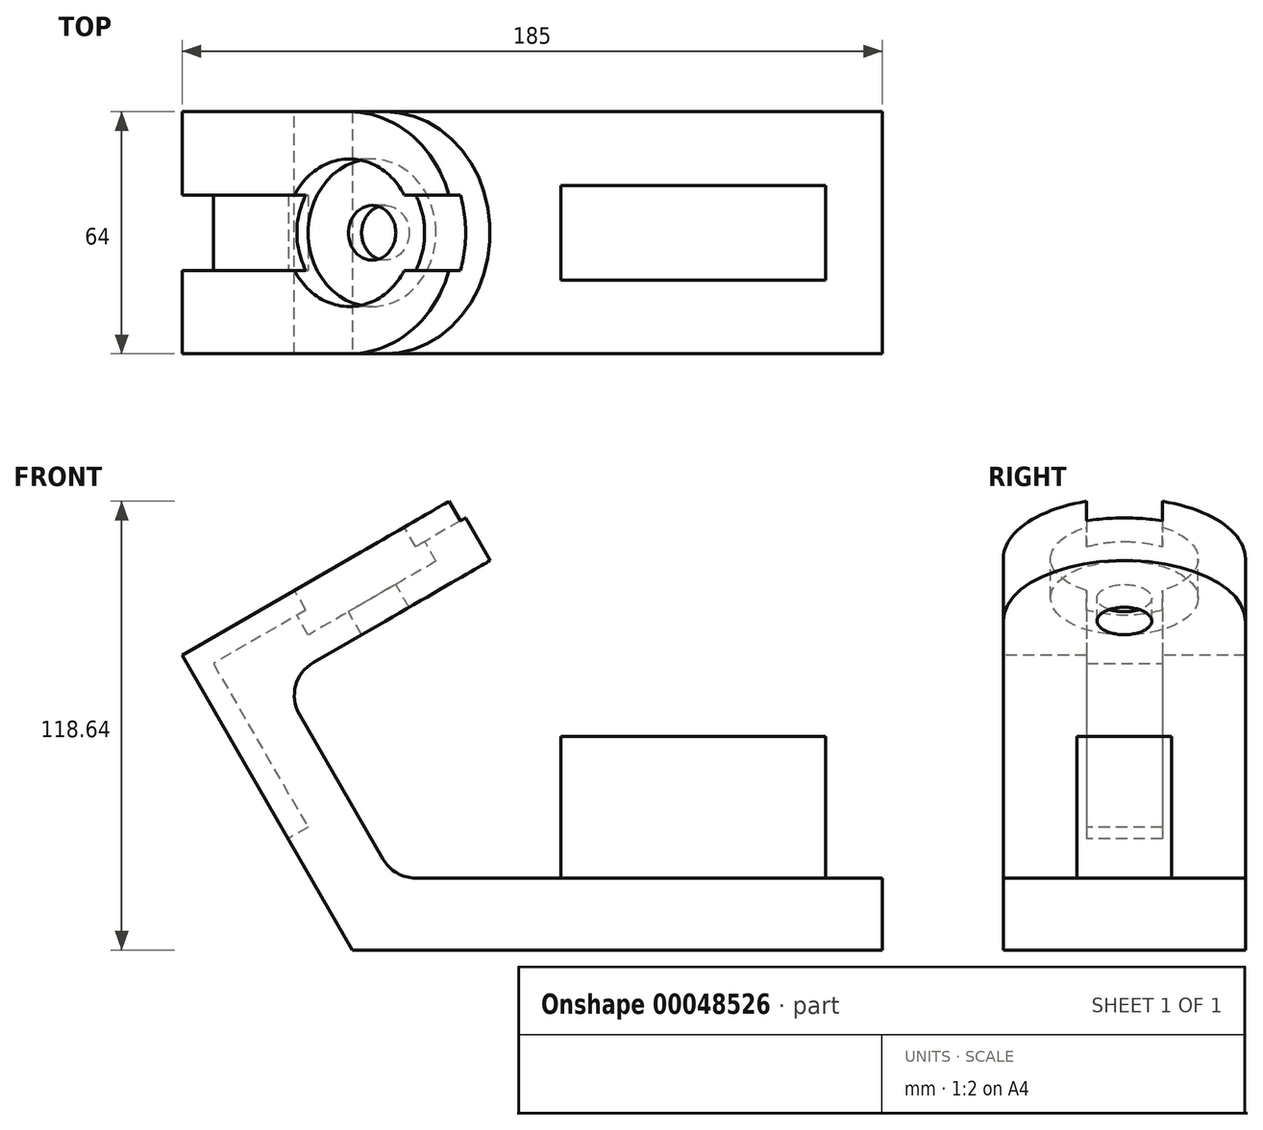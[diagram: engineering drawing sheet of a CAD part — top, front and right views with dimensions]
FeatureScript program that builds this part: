
annotation { "Feature Type Name" : "Feature", "Feature Type Description" : "" }
export const myFeature = defineFeature(function(context is Context, id is Id, definition is map)
    precondition{}
    {
        {
            var Q0;
            Q0=qCreatedBy(makeId("Front.planeOp"),FACE);
            var sketch = newSketch(context, id + "F0", { "sketchPlane" : qUnion([Q0])});
            skLineSegment(sketch, "E0", {"start": v(0, 0) * mm, "end": v(-45, 77.94) * mm});
            skLineSegment(sketch, "E1", {"start": v(-45, 77.94) * mm, "end": v(26.88, 119.44) * mm});
            skLineSegment(sketch, "E2", {"start": v(0, 0) * mm, "end": v(140, 0) * mm});
            skLineSegment(sketch, "E3.0", {"start": v(-19.05, 70.99) * mm, "end": v(36.38, 102.99) * mm});
            skLineSegment(sketch, "E3.1", {"start": v(10.97, 19) * mm, "end": v(-19.05, 70.99) * mm});
            skLineSegment(sketch, "E3.2", {"start": v(10.97, 19) * mm, "end": v(140, 19) * mm});
            skLineSegment(sketch, "E4", {"start": v(26.88, 119.44) * mm, "end": v(36.38, 102.99) * mm});
            skLineSegment(sketch, "E5", {"start": v(140, 0) * mm, "end": v(140, 19) * mm});
            skSolve(sketch);
        }
        {
            var Q0;
            Q0 = qSketchRegion(id + "F0", true);
            extrude(context, id + "F1", {"entities" : qUnion([Q0]), "oppositeDirection" : true, "depth" : 64 * mm});
        }
        {
            var Q0;
            Q0=makeQuery(id+"F1.opExtrude","SWEPT_FACE",FACE,{"disambiguationData":[OSD([sQuery(id+"F0.wireOp",EDGE,"E1")])]});
            var sketch = newSketch(context, id + "F2", { "sketchPlane" : qUnion([Q0])});
            skCircle(sketch, "E6", {"center": v(51, 32) * mm, "radius": 32 * mm});
            skSolve(sketch);
        }
        {
            var Q0;
            {var subQ0=sQuery(id+"F0.wireOp",EDGE,"E1");var subQ2=sQuery(id+"F2.wireOp",EDGE,"E6");var subQ4=makeQuery(id+"F1.opExtrude","CAP_EDGE",EDGE,{"disambiguationData":[OSD([subQ0])],"isStart":false});var subQ6=makeQuery(id+"F2.imprint","INTERSECT",VERTEX,{"derivedFrom":[subQ4,subQ2]});Q0=makeQuery(id+"F2.imprint","IMPRINT",FACE,{"disambiguationData":[TD([[makeQuery(id+"F2.imprint","IMPRINT",EDGE,{"disambiguationData":[TD([[subQ6,1.0]])],"derivedFrom":subQ2}),-1.0]])]});}
            var Q1;
            {var subQ0=sQuery(id+"F0.wireOp",EDGE,"E1");var subQ1=makeQuery(id+"F1.opExtrude","CAP_EDGE",EDGE,{"disambiguationData":[OSD([subQ0])],"isStart":true});var subQ2=sQuery(id+"F2.wireOp",EDGE,"E6");var subQ3=makeQuery(id+"F2.imprint","INTERSECT",VERTEX,{"derivedFrom":[subQ1,subQ2]});Q1=makeQuery(id+"F2.imprint","IMPRINT",FACE,{"disambiguationData":[TD([[makeQuery(id+"F2.imprint","IMPRINT",EDGE,{"disambiguationData":[TD([[subQ3,-1.0]])],"derivedFrom":subQ2}),-1.0]])]});}
            extrude(context, id + "F3", {"entities" : qUnion([Q0, Q1]), "operationType" : NewBodyOperationType.REMOVE, "oppositeDirection" : true, "depth" : 25 * mm});
        }
        {
            var Q0;
            Q0=makeQuery(id+"F1.opExtrude","SWEPT_FACE",FACE,{"disambiguationData":[OSD([sQuery(id+"F0.wireOp",EDGE,"E1")])]});
            var sketch = newSketch(context, id + "F4", { "sketchPlane" : qUnion([Q0])});
            skCircle(sketch, "E7", {"center": v(51, 32) * mm, "radius": 19.5 * mm});
            skCircle(sketch, "E8", {"center": v(51, 32) * mm, "radius": 6 * mm});
            skSolve(sketch);
        }
        {
            var Q0;
            Q0 = qSketchRegion(id + "F4", true);
            var Q1;
            Q1=makeQuery(id+"F4.imprint","IMPRINT",FACE,{"disambiguationData":[TD([[makeQuery(id+"F4.imprint","IMPRINT",EDGE,{"derivedFrom":sQuery(id+"F4.wireOp",EDGE,"E8")}),1.0]])]});
            var Q2;
            Q2=makeQuery(id+"F4.imprint","IMPRINT",FACE,{"disambiguationData":[TD([[makeQuery(id+"F4.imprint","IMPRINT",EDGE,{"derivedFrom":sQuery(id+"F4.wireOp",EDGE,"E7")}),1.0]])]});
            extrude(context, id + "F5", {"entities" : qUnion([Q0, Q1, Q2]), "operationType" : NewBodyOperationType.REMOVE, "oppositeDirection" : true, "depth" : 12 * mm});
        }
        {
            var Q0;
            Q0=makeQuery(id+"F5.boolean.opBoolean","COPY",FACE,{"derivedFrom":makeQuery(id+"F5.opExtrude","CAP_FACE",FACE,{"disambiguationData":[OSD([sQuery(id+"F4.wireOp",EDGE,"E7")])],"isStart":false})});
            var sketch = newSketch(context, id + "F6", { "sketchPlane" : qUnion([Q0])});
            skCircle(sketch, "E9", {"center": v(51, 32) * mm, "radius": 7.23 * mm});
            skSolve(sketch);
        }
        {
            var Q0;
            Q0=makeQuery(id+"F6.imprint","IMPRINT",FACE,{"disambiguationData":[TD([[makeQuery(id+"F6.imprint","IMPRINT",EDGE,{"derivedFrom":sQuery(id+"F6.wireOp",EDGE,"E9")}),1.0]])]});
            var Q1;
            Q1=makeQuery(id+"F1.opExtrude","SWEPT_FACE",FACE,{"disambiguationData":[OSD([sQuery(id+"F0.wireOp",EDGE,"E3.0")])]});
            extrude(context, id + "F7", {"entities" : qUnion([Q0]), "operationType" : NewBodyOperationType.REMOVE, "endBound" : BoundingType.UP_TO_SURFACE, "oppositeDirection" : true, "endBoundEntityFace" : qUnion([Q1]), "depth" : 25 * mm});
        }
        {
            var Q0;
            Q0=makeQuery(id+"F1.opExtrude","SWEPT_FACE",FACE,{"disambiguationData":[OSD([sQuery(id+"F0.wireOp",EDGE,"E0")])]});
            var sketch = newSketch(context, id + "F8", { "sketchPlane" : qUnion([Q0])});
            skLineSegment(sketch, "E10.bottom", {"start": v(-42, 90) * mm, "end": v(-22, 90) * mm});
            skLineSegment(sketch, "E10.top", {"start": v(-42, 34) * mm, "end": v(-22, 34) * mm});
            skLineSegment(sketch, "E10.left", {"start": v(-42, 90) * mm, "end": v(-42, 34) * mm});
            skLineSegment(sketch, "E10.right", {"start": v(-22, 90) * mm, "end": v(-22, 34) * mm});
            skSolve(sketch);
        }
        {
            var Q0;
            Q0 = qSketchRegion(id + "F8", true);
            extrude(context, id + "F9", {"entities" : qUnion([Q0]), "operationType" : NewBodyOperationType.REMOVE, "oppositeDirection" : true, "depth" : 6 * mm});
        }
        {
            var Q0;
            Q0=makeQuery(id+"F1.opExtrude","SWEPT_FACE",FACE,{"disambiguationData":[OSD([sQuery(id+"F0.wireOp",EDGE,"E1")])]});
            var sketch = newSketch(context, id + "F10", { "sketchPlane" : qUnion([Q0])});
            skPoint(sketch, "E11.oppositeSnap0", {"position": v(3, 22) * mm});
            skLineSegment(sketch, "E11.bottom", {"start": v(0, 42) * mm, "end": v(88.78, 42) * mm});
            skLineSegment(sketch, "E11.top", {"start": v(0, 22) * mm, "end": v(88.78, 22) * mm});
            skLineSegment(sketch, "E11.left", {"start": v(0, 42) * mm, "end": v(0, 22) * mm});
            skLineSegment(sketch, "E11.right", {"start": v(88.78, 42) * mm, "end": v(88.78, 22) * mm});
            skSolve(sketch);
        }
        {
            var Q0;
            Q0 = qSketchRegion(id + "F10", true);
            extrude(context, id + "F11", {"entities" : qUnion([Q0]), "operationType" : NewBodyOperationType.REMOVE, "oppositeDirection" : true, "depth" : 6 * mm});
        }
        {
            var Q0;
            Q0=makeQuery(id+"F1.opExtrude","SWEPT_EDGE",EDGE,{"disambiguationData":[OSD([sQuery(id+"F0.wireOp",EDGE,"E3.0"),sQuery(id+"F0.wireOp",EDGE,"E3.1")])]});
            fillet(context, id + "F12", {"entities" : qUnion([Q0]), "radius" : 10 * mm, "tangentPropagation" : true, "allowEdgeOverflow" : false});
        }
        {
            var Q0;
            Q0=makeQuery(id+"F1.opExtrude","SWEPT_EDGE",EDGE,{"disambiguationData":[OSD([sQuery(id+"F0.wireOp",EDGE,"E3.1"),sQuery(id+"F0.wireOp",EDGE,"E3.2")])]});
            fillet(context, id + "F13", {"entities" : qUnion([Q0]), "radius" : 10 * mm, "tangentPropagation" : true, "allowEdgeOverflow" : false});
        }
        {
            var Q0;
            Q0=makeQuery(id+"F1.opExtrude","SWEPT_FACE",FACE,{"disambiguationData":[OSD([sQuery(id+"F0.wireOp",EDGE,"E3.2")])]});
            var sketch = newSketch(context, id + "F14", { "sketchPlane" : qUnion([Q0])});
            skLineSegment(sketch, "E12.bottom", {"start": v(125, 44.5) * mm, "end": v(55, 44.5) * mm});
            skLineSegment(sketch, "E12.top", {"start": v(125, 19.5) * mm, "end": v(55, 19.5) * mm});
            skLineSegment(sketch, "E12.left", {"start": v(125, 44.5) * mm, "end": v(125, 19.5) * mm});
            skLineSegment(sketch, "E12.right", {"start": v(55, 44.5) * mm, "end": v(55, 19.5) * mm});
            skSolve(sketch);
        }
        {
            var Q0;
            Q0 = qSketchRegion(id + "F14", true);
            extrude(context, id + "F15", {"entities" : qUnion([Q0]), "operationType" : NewBodyOperationType.ADD, "depth" : 37.5 * mm});
        }
    });
